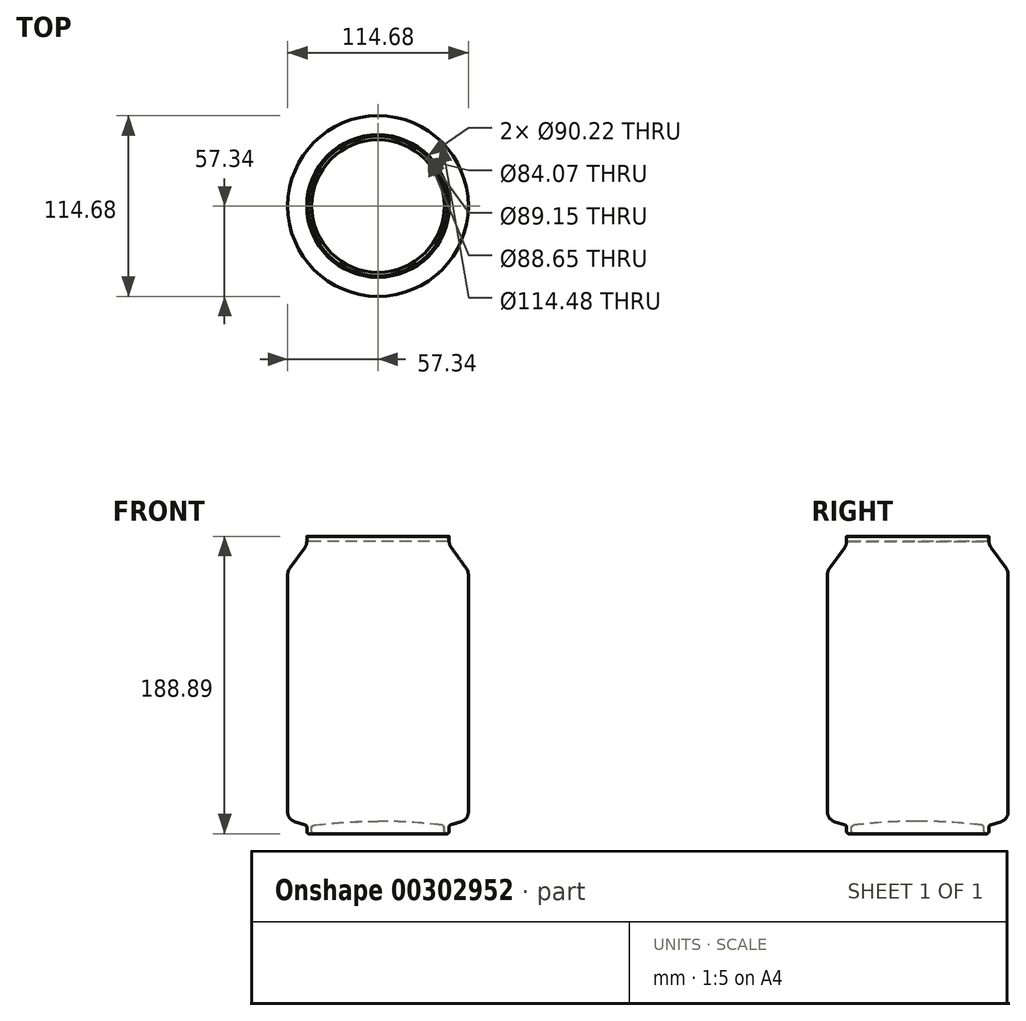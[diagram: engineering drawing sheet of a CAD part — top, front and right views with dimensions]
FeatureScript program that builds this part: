
annotation { "Feature Type Name" : "Feature", "Feature Type Description" : "" }
export const myFeature = defineFeature(function(context is Context, id is Id, definition is map)
    precondition{}
    {
        {
            var Q0;
            Q0=qCreatedBy(makeId("Front.planeOp"),FACE);
            var sketch = newSketch(context, id + "F0", { "sketchPlane" : qUnion([Q0])});
            skLineSegment(sketch, "E0", {"start": v(-43.62, -5.38) * mm, "end": v(-43.62, -5.38) * mm});
            skLineSegment(sketch, "E1", {"start": v(-45.21, -3.8) * mm, "end": v(-45.21, -1.18) * mm});
            skArc(sketch, "E2", {"start": v(-40.65, 0) * mm, "mid": v(-20.36, 1.9) * mm, "end": v(0, 2.53) * mm});
            skLineSegment(sketch, "E3", {"start": v(-46.34, 0.34) * mm, "end": v(-52.82, 2.29) * mm});
            skLineSegment(sketch, "E4", {"start": v(-57.34, 8.37) * mm, "end": v(-57.34, 159.38) * mm});
            skLineSegment(sketch, "E5", {"start": v(-56.15, 163.1) * mm, "end": v(-46.4, 176.62) * mm});
            skLineSegment(sketch, "E6", {"start": v(-45.21, 180.33) * mm, "end": v(-45.21, 183.25) * mm});
            skLineSegment(sketch, "E7", {"start": v(-44.96, 183.5) * mm, "end": v(-44.83, 183.5) * mm});
            skLineSegment(sketch, "E8", {"start": v(-44.58, 183.25) * mm, "end": v(-44.58, 180.58) * mm});
            skLineSegment(sketch, "E9", {"start": v(-44.32, 180.33) * mm, "end": v(0, 180.33) * mm});
            skLineSegment(sketch, "E10", {"start": v(0, 180.33) * mm, "end": v(0, 2.53) * mm});
            skPoint(sketch, "E11.visualSharp", {"position": v(-57.34, 161.43) * mm});
            skArc(sketch, "E11.filletArc", {"start": v(-56.15, 163.1) * mm, "mid": v(-57.04, 161.33) * mm, "end": v(-57.34, 159.38) * mm});
            skPoint(sketch, "E12.visualSharp", {"position": v(-57.34, 3.65) * mm});
            skArc(sketch, "E12.filletArc", {"start": v(-57.34, 8.37) * mm, "mid": v(-56.09, 4.58) * mm, "end": v(-52.82, 2.29) * mm});
            skPoint(sketch, "E13.visualSharp", {"position": v(-42.04, -0.18) * mm});
            skLineSegment(sketch, "E14", {"start": v(-42.04, -3.8) * mm, "end": v(-42.04, -1.58) * mm});
            skArc(sketch, "E15.filletArc", {"start": v(-40.65, 0) * mm, "mid": v(-41.64, -0.52) * mm, "end": v(-42.04, -1.58) * mm});
            skPoint(sketch, "E16.visualSharp", {"position": v(-42.04, -5.38) * mm});
            skArc(sketch, "E16.filletArc", {"start": v(-43.62, -5.38) * mm, "mid": v(-42.5, -4.92) * mm, "end": v(-42.04, -3.8) * mm});
            skPoint(sketch, "E17.visualSharp", {"position": v(-45.21, -5.38) * mm});
            skArc(sketch, "E17.filletArc", {"start": v(-45.21, -3.8) * mm, "mid": v(-44.75, -4.92) * mm, "end": v(-43.62, -5.38) * mm});
            skPoint(sketch, "E18.visualSharp", {"position": v(-45.21, 0) * mm});
            skArc(sketch, "E18.filletArc", {"start": v(-45.21, -1.18) * mm, "mid": v(-45.53, -0.23) * mm, "end": v(-46.34, 0.34) * mm});
            skPoint(sketch, "E19.visualSharp", {"position": v(-45.21, 178.28) * mm});
            skArc(sketch, "E19.filletArc", {"start": v(-46.4, 176.62) * mm, "mid": v(-45.52, 178.38) * mm, "end": v(-45.21, 180.33) * mm});
            skPoint(sketch, "E20.visualSharp", {"position": v(-45.21, 183.5) * mm});
            skArc(sketch, "E20.filletArc", {"start": v(-44.96, 183.5) * mm, "mid": v(-45.14, 183.43) * mm, "end": v(-45.21, 183.25) * mm});
            skPoint(sketch, "E21.visualSharp", {"position": v(-44.58, 183.5) * mm});
            skArc(sketch, "E21.filletArc", {"start": v(-44.58, 183.25) * mm, "mid": v(-44.65, 183.43) * mm, "end": v(-44.83, 183.5) * mm});
            skPoint(sketch, "E22.visualSharp", {"position": v(-44.58, 180.33) * mm});
            skArc(sketch, "E22.filletArc", {"start": v(-44.58, 180.58) * mm, "mid": v(-44.5, 180.4) * mm, "end": v(-44.32, 180.33) * mm});
            skSolve(sketch);
        }
        {
            var Q0;
            Q0=makeQuery(id+"F0.imprint","IMPRINT",FACE,{"disambiguationData":[TD([[makeQuery(id+"F0.imprint","IMPRINT",EDGE,{"derivedFrom":sQuery(id+"F0.wireOp",EDGE,"E1")}),-1.0]])]});
            var Q1;
            Q1=sQuery(id+"F0.wireOp",EDGE,"E10");
            revolve(context, id + "F1", {"entities" : qUnion([Q0]), "axis" : qUnion([Q1]), "revolveType" : RevolveType.FULL});
        }
        {
            var Q0;
            Q0=makeQuery(id+"F1.opRevolve","SWEPT_FACE",FACE,{"disambiguationData":[OSD([sQuery(id+"F0.wireOp",EDGE,"E9")])]});
            var Q1;
            Q1=makeQuery(id+"F1.opRevolve","SWEPT_BODY",BODY,{"disambiguationData":[OSD([sQuery(id+"F0.wireOp",EDGE,"E1"),sQuery(id+"F0.wireOp",EDGE,"E2"),sQuery(id+"F0.wireOp",EDGE,"E3"),sQuery(id+"F0.wireOp",EDGE,"E4"),sQuery(id+"F0.wireOp",EDGE,"E5"),sQuery(id+"F0.wireOp",EDGE,"E6"),sQuery(id+"F0.wireOp",EDGE,"E7"),sQuery(id+"F0.wireOp",EDGE,"E8"),sQuery(id+"F0.wireOp",EDGE,"E9"),sQuery(id+"F0.wireOp",EDGE,"E10"),sQuery(id+"F0.wireOp",EDGE,"E11.filletArc"),sQuery(id+"F0.wireOp",EDGE,"E12.filletArc"),sQuery(id+"F0.wireOp",EDGE,"E14"),sQuery(id+"F0.wireOp",EDGE,"E15.filletArc"),sQuery(id+"F0.wireOp",EDGE,"E16.filletArc"),sQuery(id+"F0.wireOp",EDGE,"E17.filletArc"),sQuery(id+"F0.wireOp",EDGE,"E18.filletArc"),sQuery(id+"F0.wireOp",EDGE,"E19.filletArc"),sQuery(id+"F0.wireOp",EDGE,"E20.filletArc"),sQuery(id+"F0.wireOp",EDGE,"E21.filletArc"),sQuery(id+"F0.wireOp",EDGE,"E22.filletArc")])]});
            shell(context, id + "F2", {"entities" : qUnion([Q0]), "parts" : qUnion([Q1]), "thickness" : 0.1 * mm});
        }
    });
